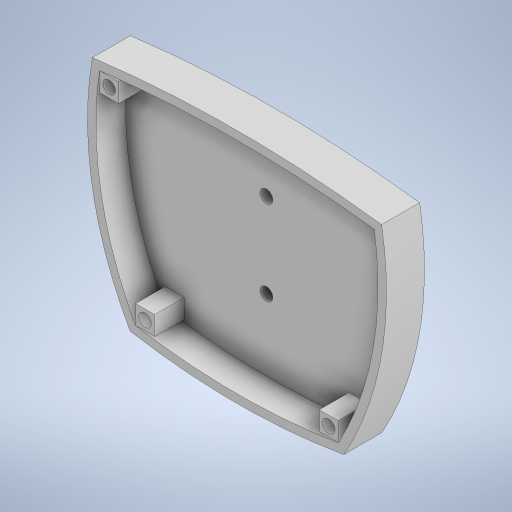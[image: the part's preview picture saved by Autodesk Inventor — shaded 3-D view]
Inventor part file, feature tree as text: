
AUTODESK INVENTOR PART (.ipt)
format: ipt  version: 2023 (Build 270158000, 158)  size: 307,200 bytes
history: native  units: in
note: dims shown in document units (in); Inventor stores cm internally (conversion verified against a paired STEP export)
features: extrude x5, sketch x1
ambient origin geometry x8: Origin, YZ Plane, XZ Plane, XY Plane, X Axis, Y Axis, Z Axis, Center Point
bodies: Body1 (feature_tree)
feature tree (6):
  sketch  "Sketch1"  dims[d0=0.9055in d1=0.9843in d4=2.5591in d6=1.8898in d7=1.2795in d8=1.2795in d9=0.0787in d10=0.0787in d11=0.0787in d15=0.1969in d19=0.0678in d33=0.1772in d34=0.1772in d35=0.1772in d36=0.1772in d37=0.1772in d38=0.1772in d43=0.1181in d44=0.1181in d45=0.0787in d46=0.0in d47=0.2756in d48=0.0in d49=0.0787in d50=0.0in d51=0.3937in d52=0.3937in d53=0.1181in d54=0.1181in d55=0.0in d56=0.0in d57=0.0in d58=0.0in]
  extrude  "Extrusion5"  Depth=0.3937in
  extrude  "Extrusion6"  Depth=0.3937in
  extrude  "Extrusion7"  Depth=1.8898in
  extrude  "Extrusion8"  Depth=0.3937in
  extrude  "Extrusion9"  Depth=0.3937in
